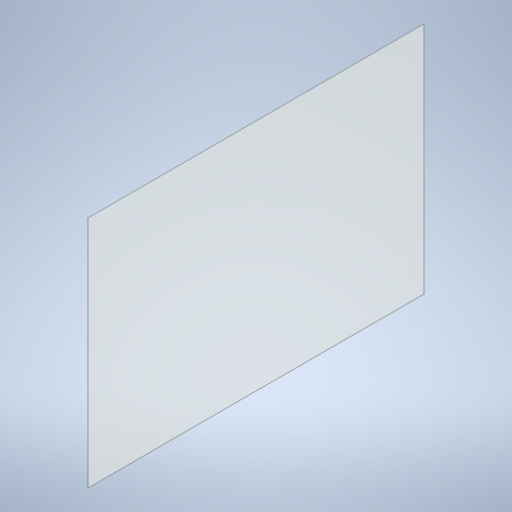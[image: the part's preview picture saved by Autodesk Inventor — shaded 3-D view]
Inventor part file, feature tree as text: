
AUTODESK INVENTOR PART (.ipt)
format: ipt  version: 2024 (Build 280153000, 153)  size: 215,040 bytes
history: native  units: in
note: dims shown in document units (in); Inventor stores cm internally (conversion verified against a paired STEP export)
features: extrude x1, sketch x1
ambient origin geometry x8: Origin, YZ Plane, XZ Plane, XY Plane, X Axis, Y Axis, Z Axis, Center Point
bodies: Solid1 (feature_tree)
feature tree (2):
  extrude  "Extrusion1"  Depth=208.632in
  sketch  "Sketch1"  dims[d2=300.0in d3=208.632in d4=0.5in d5=0.0in]
